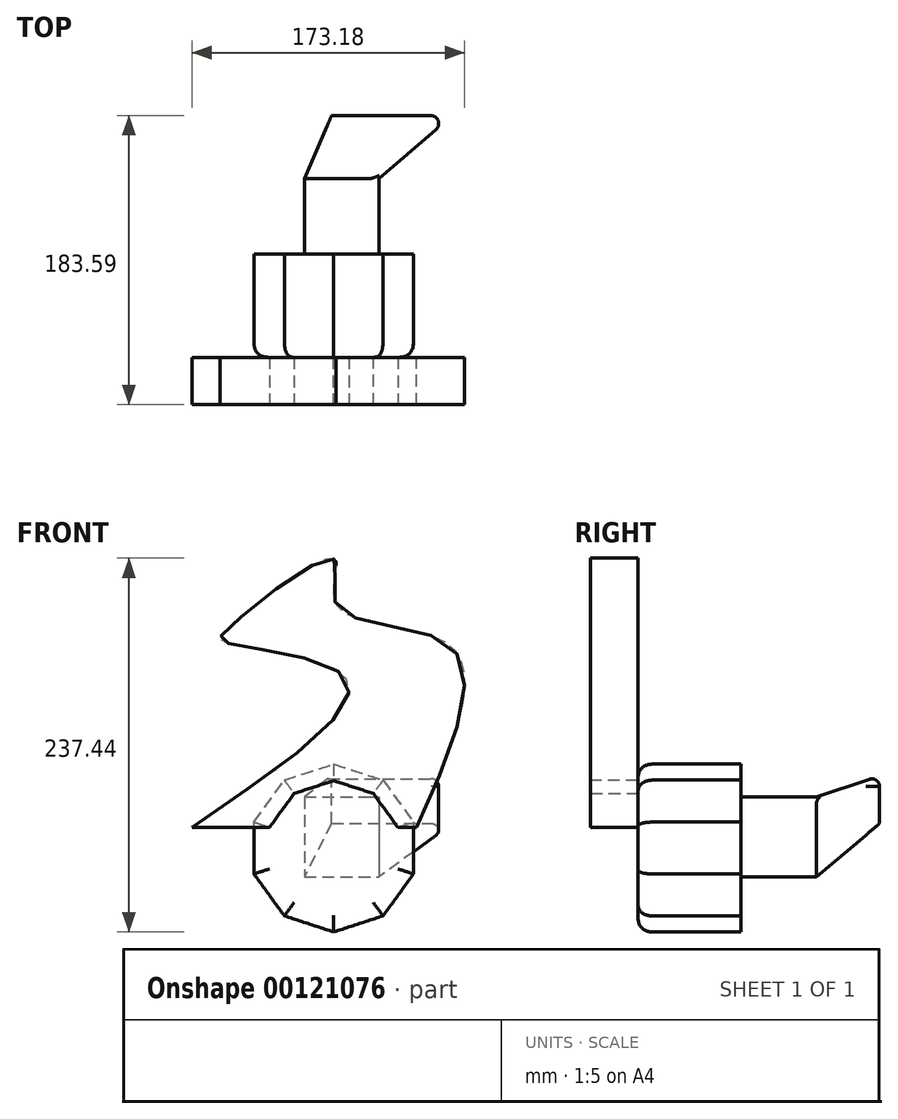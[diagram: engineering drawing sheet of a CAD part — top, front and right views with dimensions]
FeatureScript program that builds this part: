
annotation { "Feature Type Name" : "Feature", "Feature Type Description" : "" }
export const myFeature = defineFeature(function(context is Context, id is Id, definition is map)
    precondition{}
    {
        {
            var Q0;
            Q0=qCreatedBy(makeId("Top.planeOp"),FACE);
            var sketch = newSketch(context, id + "F0", { "sketchPlane" : qUnion([Q0])});
            skLineSegment(sketch, "E0.bottom", {"start": v(0, 0) * mm, "end": v(47.42, 0) * mm});
            skLineSegment(sketch, "E0.top", {"start": v(0, -47.94) * mm, "end": v(47.42, -47.94) * mm});
            skLineSegment(sketch, "E0.left", {"start": v(0, 0) * mm, "end": v(0, -47.94) * mm});
            skLineSegment(sketch, "E0.right", {"start": v(47.42, 0) * mm, "end": v(47.42, -47.94) * mm});
            skSolve(sketch);
        }
        {
            var Q0;
            Q0=makeQuery(id+"F0.imprint","IMPRINT",FACE,{"disambiguationData":[TD([[makeQuery(id+"F0.imprint","IMPRINT",EDGE,{"derivedFrom":sQuery(id+"F0.wireOp",EDGE,"E0.bottom")}),-1.0]])]});
            extrude(context, id + "F1", {"entities" : qUnion([Q0]), "depth" : 50.8 * mm});
        }
        {
            var Q0;
            Q0=makeQuery(id+"F1.opExtrude","SWEPT_FACE",FACE,{"disambiguationData":[OSD([sQuery(id+"F0.wireOp",EDGE,"E0.top")])]});
            var sketch = newSketch(context, id + "F2", { "sketchPlane" : qUnion([Q0])});
            skCircle(sketch, "E1.cCircle", {"center": v(18.68, 18.37) * mm, "radius": 50.7 * mm, "construction": true});
            skLineSegment(sketch, "E1.0", {"start": v(-32.02, 1.9) * mm, "end": v(-32.02, 34.85) * mm});
            skLineSegment(sketch, "E1.1", {"start": v(-32.02, 34.85) * mm, "end": v(-12.65, 61.5) * mm});
            skLineSegment(sketch, "E1.2", {"start": v(-12.65, 61.5) * mm, "end": v(18.68, 71.68) * mm});
            skLineSegment(sketch, "E1.3", {"start": v(18.68, 71.68) * mm, "end": v(50, 61.5) * mm});
            skLineSegment(sketch, "E1.4", {"start": v(50, 61.5) * mm, "end": v(69.37, 34.85) * mm});
            skLineSegment(sketch, "E1.5", {"start": v(69.37, 34.85) * mm, "end": v(69.37, 1.9) * mm});
            skLineSegment(sketch, "E1.6", {"start": v(69.37, 1.9) * mm, "end": v(50, -24.75) * mm});
            skLineSegment(sketch, "E1.7", {"start": v(50, -24.75) * mm, "end": v(18.68, -34.93) * mm});
            skLineSegment(sketch, "E1.8", {"start": v(18.68, -34.93) * mm, "end": v(-12.65, -24.75) * mm});
            skLineSegment(sketch, "E1.9", {"start": v(-12.65, -24.75) * mm, "end": v(-32.02, 1.9) * mm});
            skPoint(sketch, "E1.0.midPoint", {"position": v(-32.02, 18.37) * mm});
            skSolve(sketch);
        }
        {
            var Q0;
            Q0 = qSketchRegion(id + "F2", true);
            extrude(context, id + "F3", {"entities" : qUnion([Q0]), "operationType" : NewBodyOperationType.ADD, "depth" : 30 * mm});
        }
        {
            var Q0;
            Q0=makeQuery(id+"F3.opExtrude","CAP_FACE",FACE,{"disambiguationData":[OSD([sQuery(id+"F2.wireOp",EDGE,"E1.0"),sQuery(id+"F2.wireOp",EDGE,"E1.1"),sQuery(id+"F2.wireOp",EDGE,"E1.2"),sQuery(id+"F2.wireOp",EDGE,"E1.3"),sQuery(id+"F2.wireOp",EDGE,"E1.4"),sQuery(id+"F2.wireOp",EDGE,"E1.5"),sQuery(id+"F2.wireOp",EDGE,"E1.6"),sQuery(id+"F2.wireOp",EDGE,"E1.7"),sQuery(id+"F2.wireOp",EDGE,"E1.8"),sQuery(id+"F2.wireOp",EDGE,"E1.9")])],"isStart":false});
            var sketch = newSketch(context, id + "F4", { "sketchPlane" : qUnion([Q0])});
            skLineSegment(sketch, "E2.0", {"start": v(-8.6, -21.8) * mm, "end": v(-27.97, 4.84) * mm});
            skLineSegment(sketch, "E3.0", {"start": v(-4.56, -18.87) * mm, "end": v(-23.93, 7.78) * mm});
            skSolve(sketch);
        }
        {
            var Q0;
            Q0=makeQuery(id+"F4.imprint","IMPRINT",FACE,{"disambiguationData":[TD([[makeQuery(id+"F4.imprint","IMPRINT",EDGE,{"derivedFrom":makeQuery(id+"F3.opExtrude","CAP_EDGE",EDGE,{"disambiguationData":[OSD([sQuery(id+"F2.wireOp",EDGE,"E1.0")])],"isStart":false})}),-1.0]])]});
            extrude(context, id + "F5", {"entities" : qUnion([Q0]), "operationType" : NewBodyOperationType.ADD, "depth" : 35.65 * mm});
        }
        {
            var Q0;
            Q0=makeQuery(id+"F5.opExtrude","CAP_FACE",FACE,{"disambiguationData":[OSD([sQuery(id+"F2.wireOp",EDGE,"E1.0"),sQuery(id+"F2.wireOp",EDGE,"E1.1"),sQuery(id+"F2.wireOp",EDGE,"E1.2"),sQuery(id+"F2.wireOp",EDGE,"E1.3"),sQuery(id+"F2.wireOp",EDGE,"E1.4"),sQuery(id+"F2.wireOp",EDGE,"E1.5"),sQuery(id+"F2.wireOp",EDGE,"E1.6"),sQuery(id+"F2.wireOp",EDGE,"E1.7"),sQuery(id+"F2.wireOp",EDGE,"E1.8"),sQuery(id+"F2.wireOp",EDGE,"E1.9")])],"isStart":false});
            fillet(context, id + "F6", {"entities" : qUnion([Q0]), "radius" : 10 * mm, "tangentPropagation" : true, "rho" : 0.5, "crossSection" : FilletCrossSection.CONIC, "allowEdgeOverflow" : false});
        }
        {
            var Q0;
            Q0=makeQuery(id+"F1.opExtrude","SWEPT_FACE",FACE,{"disambiguationData":[OSD([sQuery(id+"F0.wireOp",EDGE,"E0.bottom")])]});
            cPlane(context, id + "F7", {"entities" : qUnion([Q0]), "cplaneType" : CPlaneType.OFFSET, "offset" : 40 * mm, "width" : 150 * mm, "height" : 150 * mm});
        }
        {
            var Q0;
            Q0=qCreatedBy(id+"F7.planeOp",FACE);
            var sketch = newSketch(context, id + "F8", { "sketchPlane" : qUnion([Q0])});
            skLineSegment(sketch, "E4.bottom", {"start": v(-17.33, 33.96) * mm, "end": v(-93.84, 33.96) * mm});
            skLineSegment(sketch, "E4.top", {"start": v(-17.33, 64.34) * mm, "end": v(-93.84, 64.34) * mm});
            skLineSegment(sketch, "E4.left", {"start": v(-17.33, 33.96) * mm, "end": v(-17.33, 64.34) * mm});
            skLineSegment(sketch, "E4.right", {"start": v(-93.84, 33.96) * mm, "end": v(-93.84, 64.34) * mm});
            skSolve(sketch);
        }
        {
            var Q1;
            Q1=makeQuery(id+"F8.imprint","IMPRINT",FACE,{"disambiguationData":[TD([[makeQuery(id+"F8.imprint","IMPRINT",EDGE,{"derivedFrom":sQuery(id+"F8.wireOp",EDGE,"E4.bottom")}),-1.0]])]});
            var Q2;
            Q2=makeQuery(id+"F1.opExtrude","SWEPT_FACE",FACE,{"disambiguationData":[OSD([sQuery(id+"F0.wireOp",EDGE,"E0.bottom")])]});
            loft(context, id + "F9", {"operationType" : NewBodyOperationType.ADD, "sheetProfilesArray" : [{ "sheetProfileEntities" : qUnion([Q1]) }, { "sheetProfileEntities" : qUnion([Q2]) }]});
        }
        {
            var Q0;
            Q0=makeQuery(id+"F9.opLoft","MID_CAP_EDGE",EDGE,{"disambiguationData":[OSD([sQuery(id+"F8.wireOp",EDGE,"E4.bottom"),sQuery(id+"F8.wireOp",EDGE,"E4.top"),sQuery(id+"F8.wireOp",EDGE,"E4.right")])],"capPos":0.0});
            fillet(context, id + "F10", {"entities" : qUnion([Q0]), "radius" : 5 * mm, "tangentPropagation" : true, "allowEdgeOverflow" : false});
        }
        {
            var Q0;
            Q0=makeQuery(id+"F9.opLoft","MID_CAP_EDGE",EDGE,{"disambiguationData":[OSD([sQuery(id+"F8.wireOp",EDGE,"E4.top"),sQuery(id+"F8.wireOp",EDGE,"E4.left"),sQuery(id+"F8.wireOp",EDGE,"E4.right")])],"capPos":0.0});
            fillet(context, id + "F11", {"entities" : qUnion([Q0]), "radius" : 5 * mm, "tangentPropagation" : true, "allowEdgeOverflow" : false});
        }
        {
            var Q0;
            Q0=makeQuery(id+"F5.opExtrude","CAP_FACE",FACE,{"disambiguationData":[OSD([sQuery(id+"F2.wireOp",EDGE,"E1.0"),sQuery(id+"F2.wireOp",EDGE,"E1.1"),sQuery(id+"F2.wireOp",EDGE,"E1.2"),sQuery(id+"F2.wireOp",EDGE,"E1.3"),sQuery(id+"F2.wireOp",EDGE,"E1.4"),sQuery(id+"F2.wireOp",EDGE,"E1.5"),sQuery(id+"F2.wireOp",EDGE,"E1.6"),sQuery(id+"F2.wireOp",EDGE,"E1.7"),sQuery(id+"F2.wireOp",EDGE,"E1.8"),sQuery(id+"F2.wireOp",EDGE,"E1.9")])],"isStart":false});
            var sketch = newSketch(context, id + "F12", { "sketchPlane" : qUnion([Q0])});
            skLineSegment(sketch, "E5.bottom", {"start": v(-71.4, 31.6) * mm, "end": v(71.4, 31.6) * mm});
            skLineSegment(sketch, "E5.top", {"start": v(-71.4, -31.6) * mm, "end": v(71.4, -31.6) * mm});
            skLineSegment(sketch, "E5.left", {"start": v(-71.4, 31.6) * mm, "end": v(-71.4, -31.6) * mm});
            skLineSegment(sketch, "E5.right", {"start": v(71.4, 31.6) * mm, "end": v(71.4, -31.6) * mm});
            skPoint(sketch, "E5.middle", {"position": v(0, 0) * mm});
            skFitSpline(sketch, "E6", {"points": [v(-71.4, 31.6) * mm, v(25.85, 126.84) * mm, v(-51.55, 149.54) * mm, v(-50.74, 155.61) * mm, v(18.56, 202.22) * mm, v(20.18, 173.04) * mm, v(92.72, 146.7) * mm, v(71.4, 31.6) * mm], "startDerivative": vector(831.75, 561.4) * mm, "endDerivative": vector(-341.98, -766.05) * mm});
            skSolve(sketch);
        }
        {
            var Q0;
            {var subQ8=sQuery(id+"F12.wireOp",EDGE,"E6");Q0=makeQuery(id+"F12.imprint","IMPRINT",FACE,{"disambiguationData":[TD([[makeQuery(id+"F12.imprint","IMPRINT",EDGE,{"derivedFrom":subQ8}),-1.0]])]});}
            extrude(context, id + "F13", {"entities" : qUnion([Q0]), "depth" : 30 * mm});
        }
    });
